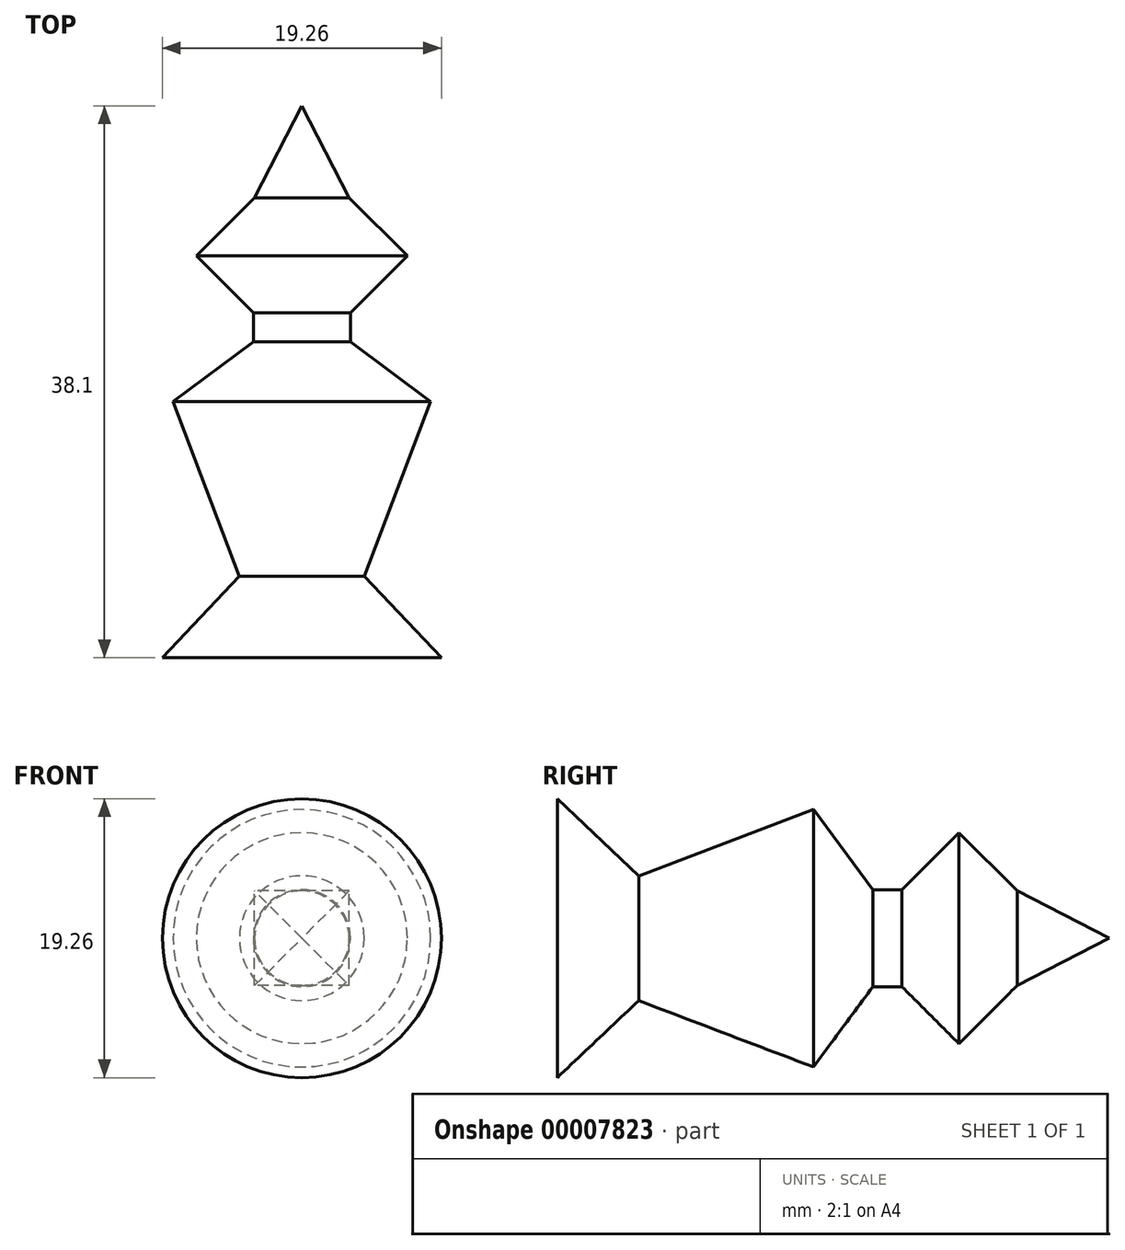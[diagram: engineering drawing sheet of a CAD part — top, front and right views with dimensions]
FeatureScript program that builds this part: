
annotation { "Feature Type Name" : "Feature", "Feature Type Description" : "" }
export const myFeature = defineFeature(function(context is Context, id is Id, definition is map)
    precondition{}
    {
        {
            var Q0;
            Q0=qCreatedBy(makeId("Top.planeOp"),FACE);
            var sketch = newSketch(context, id + "F0", { "sketchPlane" : qUnion([Q0])});
            skLineSegment(sketch, "E0", {"start": v(0, 0) * mm, "end": v(0, 27.63) * mm});
            skLineSegment(sketch, "E1", {"start": v(0, 0) * mm, "end": v(9.63, 0) * mm});
            skLineSegment(sketch, "E2", {"start": v(9.63, 0) * mm, "end": v(4.3, 5.63) * mm});
            skLineSegment(sketch, "E3", {"start": v(4.3, 5.63) * mm, "end": v(8.9, 17.69) * mm});
            skLineSegment(sketch, "E4", {"start": v(8.89, 17.69) * mm, "end": v(3.35, 21.8) * mm});
            skLineSegment(sketch, "E5", {"start": v(3.35, 21.8) * mm, "end": v(3.35, 23.8) * mm});
            skLineSegment(sketch, "E6", {"start": v(3.35, 23.8) * mm, "end": v(7.28, 27.74) * mm});
            skLineSegment(sketch, "E7", {"start": v(7.28, 27.74) * mm, "end": v(3.27, 31.75) * mm});
            skLineSegment(sketch, "E8", {"start": v(3.27, 31.75) * mm, "end": v(0, 31.75) * mm});
            skLineSegment(sketch, "E9", {"start": v(0, 31.75) * mm, "end": v(0, 0) * mm});
            skSolve(sketch);
        }
        {
            var Q0;
            {var subQ2=sQuery(id+"F0.wireOp",EDGE,"E1");Q0=makeQuery(id+"F0.imprint","IMPRINT",FACE,{"disambiguationData":[TD([[makeQuery(id+"F0.imprint","IMPRINT",EDGE,{"derivedFrom":subQ2}),1.0]])]});}
            var Q1;
            Q1=sQuery(id+"F0.wireOp",EDGE,"E0");
            revolve(context, id + "F1", {"entities" : qUnion([Q0]), "axis" : qUnion([Q1]), "revolveType" : RevolveType.FULL});
        }
        {
            var Q0;
            Q0=makeQuery(id+"F1.opRevolve","SWEPT_FACE",FACE,{"disambiguationData":[OSD([sQuery(id+"F0.wireOp",EDGE,"E8")])]});
            var sketch = newSketch(context, id + "F2", { "sketchPlane" : qUnion([Q0])});
            skLineSegment(sketch, "E10.rect.bottom", {"start": v(-3.27, -3.27) * mm, "end": v(3.27, -3.27) * mm});
            skLineSegment(sketch, "E10.rect.top", {"start": v(-3.27, 3.27) * mm, "end": v(3.27, 3.27) * mm});
            skLineSegment(sketch, "E10.rect.left", {"start": v(-3.27, -3.27) * mm, "end": v(-3.27, 3.27) * mm});
            skLineSegment(sketch, "E10.rect.right", {"start": v(3.27, -3.27) * mm, "end": v(3.27, 3.27) * mm});
            skPoint(sketch, "E10.rect.middle", {"position": v(0, 0) * mm});
            skSolve(sketch);
        }
        {
            var Q0;
            Q0 = qSketchRegion(id + "F2", true);
            extrude(context, id + "F3", {"entities" : qUnion([Q0]), "operationType" : NewBodyOperationType.ADD, "depth" : 6.35 * mm});
        }
        {
            var Q0;
            Q0=makeQuery(id+"F3.opExtrude","SWEPT_FACE",FACE,{"disambiguationData":[OSD([sQuery(id+"F2.wireOp",EDGE,"E10.rect.top")])]});
            var sketch = newSketch(context, id + "F4", { "sketchPlane" : qUnion([Q0])});
            skLineSegment(sketch, "E11", {"start": v(-3.27, 31.75) * mm, "end": v(0, 38.1) * mm});
            skLineSegment(sketch, "E12", {"start": v(0, 38.1) * mm, "end": v(3.27, 31.75) * mm});
            skSolve(sketch);
        }
        {
            var Q0;
            Q0=makeQuery(id+"F3.opExtrude","SWEPT_FACE",FACE,{"disambiguationData":[OSD([sQuery(id+"F2.wireOp",EDGE,"E10.rect.left")])]});
            var sketch = newSketch(context, id + "F5", { "sketchPlane" : qUnion([Q0])});
            skLineSegment(sketch, "E13", {"start": v(31.75, 3.27) * mm, "end": v(38.1, 0) * mm});
            skLineSegment(sketch, "E14", {"start": v(38.1, 0) * mm, "end": v(31.75, -3.27) * mm});
            skSolve(sketch);
        }
        {
            var Q0;
            {var subQ2=sQuery(id+"F5.wireOp",EDGE,"E14");Q0=makeQuery(id+"F5.imprint","IMPRINT",FACE,{"disambiguationData":[TD([[makeQuery(id+"F5.imprint","IMPRINT",EDGE,{"derivedFrom":subQ2}),1.0]])]});}
            var Q1;
            {var subQ2=sQuery(id+"F5.wireOp",EDGE,"E13");Q1=makeQuery(id+"F5.imprint","IMPRINT",FACE,{"disambiguationData":[TD([[makeQuery(id+"F5.imprint","IMPRINT",EDGE,{"derivedFrom":subQ2}),1.0]])]});}
            extrude(context, id + "F6", {"entities" : qUnion([Q0, Q1]), "operationType" : NewBodyOperationType.REMOVE, "oppositeDirection" : true, "depth" : 25.4 * mm});
        }
        {
            var Q0;
            {var subQ2=sQuery(id+"F4.wireOp",EDGE,"E11");Q0=makeQuery(id+"F4.imprint","IMPRINT",FACE,{"disambiguationData":[TD([[makeQuery(id+"F4.imprint","IMPRINT",EDGE,{"derivedFrom":subQ2}),1.0]])]});}
            var Q1;
            {var subQ2=sQuery(id+"F4.wireOp",EDGE,"E12");Q1=makeQuery(id+"F4.imprint","IMPRINT",FACE,{"disambiguationData":[TD([[makeQuery(id+"F4.imprint","IMPRINT",EDGE,{"derivedFrom":subQ2}),1.0]])]});}
            extrude(context, id + "F7", {"entities" : qUnion([Q0, Q1]), "operationType" : NewBodyOperationType.REMOVE, "oppositeDirection" : true, "depth" : 25.4 * mm});
        }
        {
            var Q0;
            {var subQ0=makeQuery(id+"F1.opRevolve","SWEPT_EDGE",EDGE,{"disambiguationData":[OSD([sQuery(id+"F0.wireOp",EDGE,"E7"),sQuery(id+"F0.wireOp",EDGE,"E8")])]});var subQ4=makeQuery(id+"F2.imprint","INTERSECT",VERTEX,{"derivedFrom":[subQ0,sQuery(id+"F2.wireOp",EDGE,"E10.rect.bottom")]});Q0=makeQuery(id+"F2.imprint","IMPRINT",FACE,{"disambiguationData":[TD([[makeQuery(id+"F2.imprint","IMPRINT",EDGE,{"disambiguationData":[TD([[subQ4,-1.0]])],"derivedFrom":subQ0}),-1.0]])]});}
            cPlane(context, id + "F8", {"entities" : qUnion([Q0]), "cplaneType" : CPlaneType.OFFSET, "offset" : 6.35 * mm, "width" : 152.4 * mm, "height" : 152.4 * mm});
        }
    });
